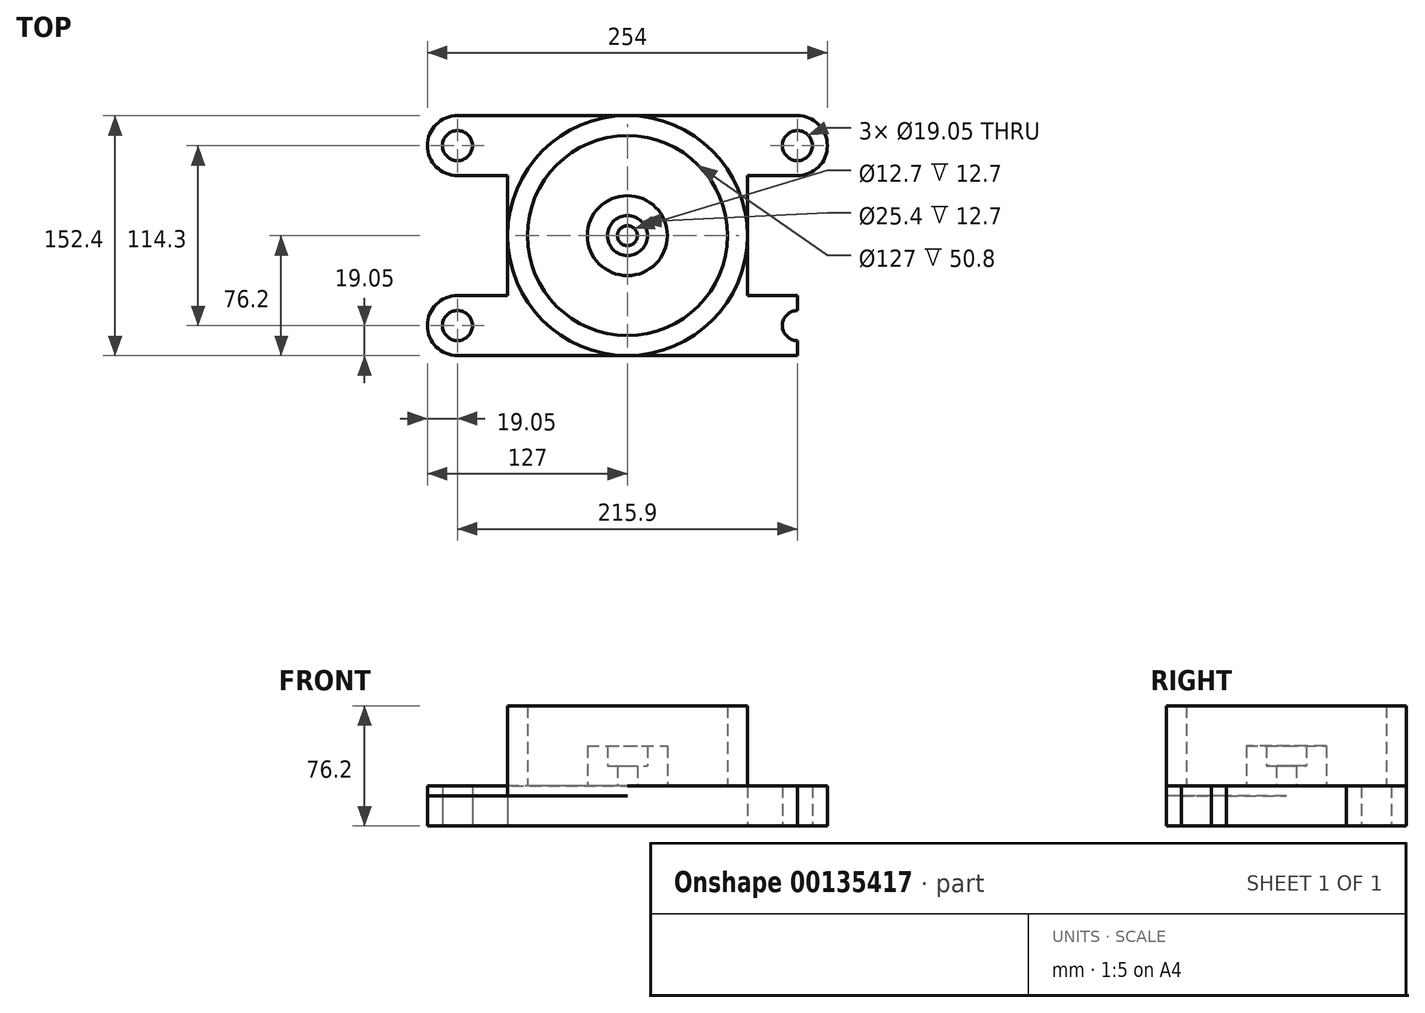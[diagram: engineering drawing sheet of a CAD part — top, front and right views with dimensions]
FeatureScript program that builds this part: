
annotation { "Feature Type Name" : "Feature", "Feature Type Description" : "" }
export const myFeature = defineFeature(function(context is Context, id is Id, definition is map)
    precondition{}
    {
        {
            var Q0;
            Q0=qCreatedBy(makeId("Front.planeOp"),FACE);
            var sketch = newSketch(context, id + "F0", { "sketchPlane" : qUnion([Q0])});
            skLineSegment(sketch, "E0", {"start": v(-6.35, 0) * mm, "end": v(-76.2, 0) * mm});
            skLineSegment(sketch, "E1", {"start": v(-76.2, 0) * mm, "end": v(-76.2, 76.2) * mm});
            skLineSegment(sketch, "E2", {"start": v(-76.2, 76.2) * mm, "end": v(-63.5, 76.2) * mm});
            skLineSegment(sketch, "E3", {"start": v(-63.5, 76.2) * mm, "end": v(-63.5, 19.05) * mm});
            skLineSegment(sketch, "E4", {"start": v(-63.5, 19.05) * mm, "end": v(-25.4, 19.05) * mm});
            skLineSegment(sketch, "E5", {"start": v(-25.4, 19.05) * mm, "end": v(-25.4, 50.8) * mm});
            skLineSegment(sketch, "E6", {"start": v(-25.4, 50.8) * mm, "end": v(-12.7, 50.8) * mm});
            skLineSegment(sketch, "E7", {"start": v(-12.7, 50.8) * mm, "end": v(-12.7, 38.1) * mm});
            skLineSegment(sketch, "E8", {"start": v(-12.7, 38.1) * mm, "end": v(-6.35, 38.1) * mm});
            skLineSegment(sketch, "E9", {"start": v(-6.35, 38.1) * mm, "end": v(-6.35, 0) * mm});
            skLineSegment(sketch, "E10", {"start": v(0, 0) * mm, "end": v(0, 76.2) * mm});
            skSolve(sketch);
        }
        {
            var Q0;
            Q0=makeQuery(id+"F0.imprint","IMPRINT",FACE,{"disambiguationData":[TD([[makeQuery(id+"F0.imprint","IMPRINT",EDGE,{"derivedFrom":sQuery(id+"F0.wireOp",EDGE,"E0")}),-1.0]])]});
            var Q1;
            Q1=sQuery(id+"F0.wireOp",EDGE,"E10");
            revolve(context, id + "F1", {"entities" : qUnion([Q0]), "axis" : qUnion([Q1]), "revolveType" : RevolveType.FULL});
        }
        {
            var Q0;
            Q0=qCreatedBy(makeId("Top.planeOp"),FACE);
            var sketch = newSketch(context, id + "F2", { "sketchPlane" : qUnion([Q0])});
            skLineSegment(sketch, "E11", {"start": v(0, -76.2) * mm, "end": v(-107.95, -76.2) * mm});
            skLineSegment(sketch, "E12", {"start": v(-107.95, -76.2) * mm, "end": v(-107.95, -66.68) * mm});
            skLineSegment(sketch, "E13", {"start": v(-107.95, -38.1) * mm, "end": v(-76.2, -38.1) * mm});
            skLineSegment(sketch, "E14", {"start": v(-76.2, -38.1) * mm, "end": v(-76.2, 0) * mm});
            skArc(sketch, "E15", {"start": v(-107.95, -38.1) * mm, "mid": v(-127, -57.15) * mm, "end": v(-107.95, -76.2) * mm});
            skCircle(sketch, "E16", {"center": v(-107.95, -57.15) * mm, "radius": 9.53 * mm});
            skLineSegment(sketch, "E17.trimOffspring", {"start": v(-107.95, -47.63) * mm, "end": v(-107.95, -38.1) * mm});
            skArc(sketch, "E18.0", {"start": v(-76.2, 0) * mm, "mid": v(-53.88, -53.88) * mm, "end": v(0, -76.2) * mm});
            skLineSegment(sketch, "E19.MirrorCS", {"start": v(-76.2, 38.1) * mm, "end": v(-76.2, 0) * mm});
            skLineSegment(sketch, "E20.MirrorCS", {"start": v(-107.95, 38.1) * mm, "end": v(-76.2, 38.1) * mm});
            skArc(sketch, "E21.MirrorCS", {"start": v(-107.95, 38.1) * mm, "mid": v(-127, 57.15) * mm, "end": v(-107.95, 76.2) * mm});
            skLineSegment(sketch, "E22.MirrorCS", {"start": v(0, 76.2) * mm, "end": v(-107.95, 76.2) * mm});
            skCircle(sketch, "E23.MirrorC", {"center": v(-107.95, 57.15) * mm, "radius": 9.53 * mm});
            skLineSegment(sketch, "E24.MirrorCS", {"start": v(0, 76.2) * mm, "end": v(107.95, 76.2) * mm});
            skLineSegment(sketch, "E25.MirrorCS", {"start": v(107.95, 38.1) * mm, "end": v(76.2, 38.1) * mm});
            skArc(sketch, "E26.MirrorCS", {"start": v(107.95, 38.1) * mm, "mid": v(127, 57.15) * mm, "end": v(107.95, 76.2) * mm});
            skCircle(sketch, "E27.MirrorC", {"center": v(107.95, 57.15) * mm, "radius": 9.53 * mm});
            skLineSegment(sketch, "E28.MirrorCS", {"start": v(76.2, 38.1) * mm, "end": v(76.2, 0) * mm});
            skLineSegment(sketch, "E29.MirrorCS", {"start": v(76.2, -38.1) * mm, "end": v(76.2, 0) * mm});
            skLineSegment(sketch, "E30.MirrorCS", {"start": v(107.95, -38.1) * mm, "end": v(76.2, -38.1) * mm});
            skArc(sketch, "E31.MirrorCS", {"start": v(107.95, -38.1) * mm, "mid": v(127, -57.15) * mm, "end": v(107.95, -76.2) * mm});
            skCircle(sketch, "E32.MirrorC", {"center": v(107.95, -57.15) * mm, "radius": 9.53 * mm});
            skLineSegment(sketch, "E33.MirrorCS", {"start": v(107.95, -76.2) * mm, "end": v(107.95, -66.68) * mm});
            skLineSegment(sketch, "E34.MirrorCS", {"start": v(107.95, -47.63) * mm, "end": v(107.95, -38.1) * mm});
            skLineSegment(sketch, "E35.MirrorCS", {"start": v(0, -76.2) * mm, "end": v(107.95, -76.2) * mm});
            skSolve(sketch);
        }
        {
            var Q0;
            Q0=makeQuery(id+"F2.imprint","IMPRINT",FACE,{"disambiguationData":[TD([[makeQuery(id+"F2.imprint","IMPRINT",EDGE,{"derivedFrom":sQuery(id+"F2.wireOp",EDGE,"E11")}),-1.0]])]});
            var Q1;
            {var subQ0=sQuery(id+"F2.wireOp",EDGE,"E12");Q1=makeQuery(id+"F2.imprint","IMPRINT",FACE,{"disambiguationData":[TD([[makeQuery(id+"F2.imprint","IMPRINT",EDGE,{"derivedFrom":subQ0}),1.0]])]});}
            extrude(context, id + "F3", {"entities" : qUnion([Q0, Q1]), "operationType" : NewBodyOperationType.ADD, "depth" : 19.05 * mm});
        }
        {
            var Q0;
            Q0=makeQuery(id+"F2.imprint","IMPRINT",FACE,{"disambiguationData":[TD([[makeQuery(id+"F2.imprint","IMPRINT",EDGE,{"derivedFrom":sQuery(id+"F2.wireOp",EDGE,"E31.MirrorCS")}),-1.0]])]});
            var Q1;
            Q1=makeQuery(id+"F2.imprint","IMPRINT",FACE,{"disambiguationData":[TD([[makeQuery(id+"F2.imprint","IMPRINT",EDGE,{"derivedFrom":sQuery(id+"F2.wireOp",EDGE,"E18.0")}),1.0]])]});
            extrude(context, id + "F4", {"entities" : qUnion([Q0, Q1]), "operationType" : NewBodyOperationType.ADD, "depth" : 25.4 * mm});
        }
    });
